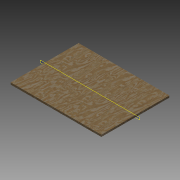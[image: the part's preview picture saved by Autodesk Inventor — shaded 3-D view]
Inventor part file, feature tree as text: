
AUTODESK INVENTOR PART (.ipt)
format: ipt  version: 2015 (Build 190159000, 159)  size: 90,112 bytes
history: native  units: in
note: dims shown in document units (in); Inventor stores cm internally (conversion verified against a paired STEP export)
features: extrude x1, plane x1, sketch x1
ambient origin geometry x8: Origin, YZ Plane, XZ Plane, XY Plane, X Axis, Y Axis, Z Axis, Center Point
bodies: Solid1 (feature_tree)
feature tree (3):
  extrude  "Extrusion1"  Depth=48.0in
  plane  "Work Plane1"
  sketch  "Sketch1"  dims[d0=36.0in d1=48.0in d2=1.0in d3=0.0in]
